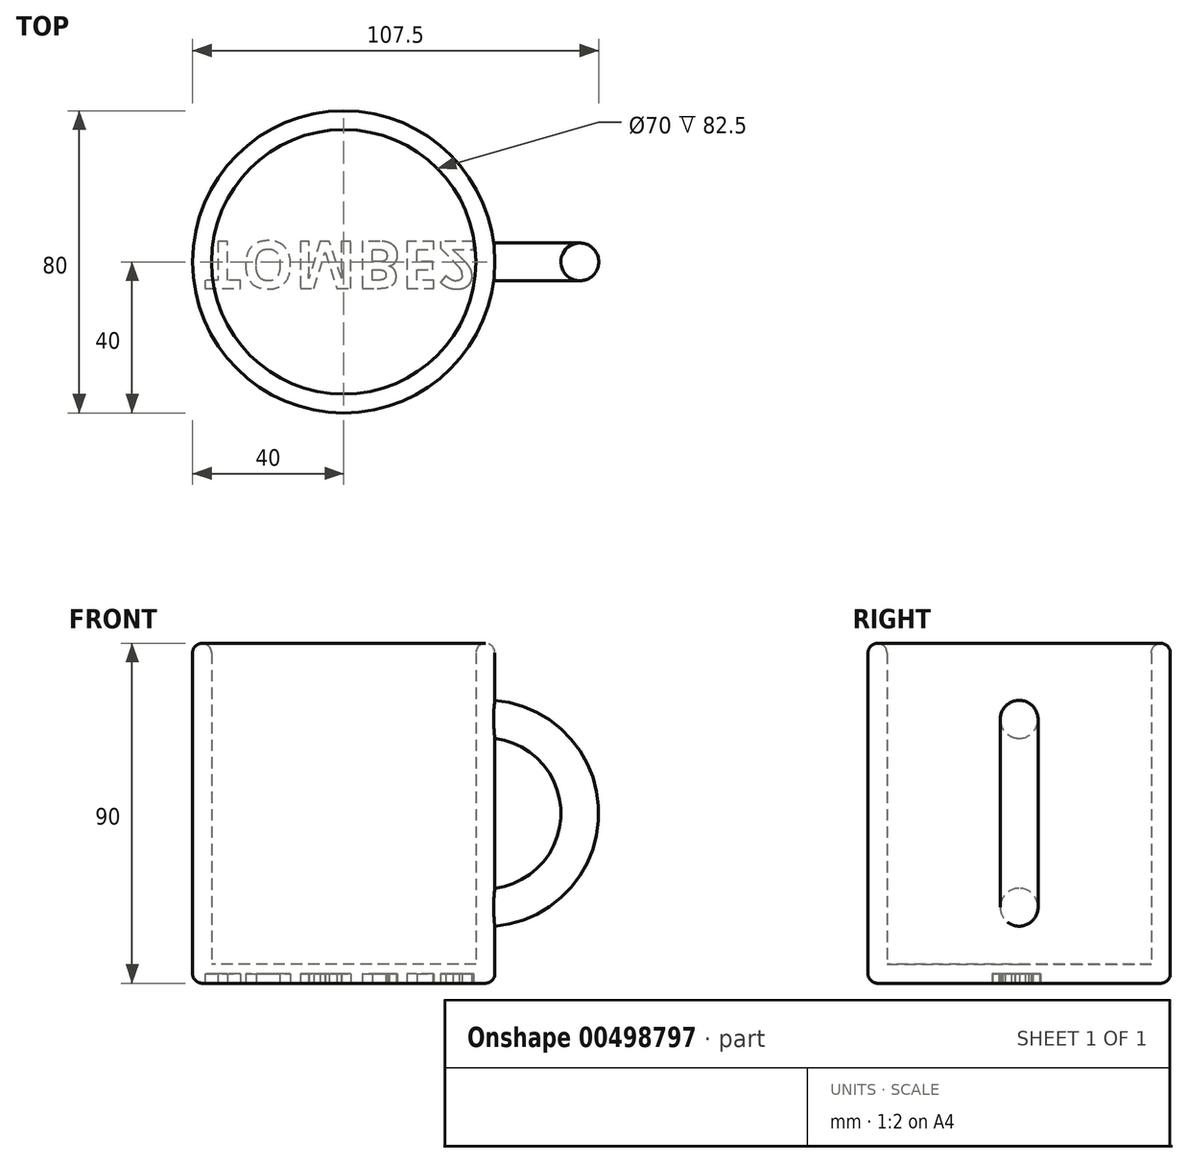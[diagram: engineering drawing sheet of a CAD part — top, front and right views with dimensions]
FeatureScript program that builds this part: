
annotation { "Feature Type Name" : "Feature", "Feature Type Description" : "" }
export const myFeature = defineFeature(function(context is Context, id is Id, definition is map)
    precondition{}
    {
        {
            var Q0;
            Q0=qCreatedBy(makeId("Top.planeOp"),FACE);
            var sketch = newSketch(context, id + "F0", { "sketchPlane" : qUnion([Q0])});
            skCircle(sketch, "E0", {"center": v(0, 0) * mm, "radius": 40 * mm});
            skSolve(sketch);
        }
        {
            var Q0;
            Q0=makeQuery(id+"F0.imprint","IMPRINT",FACE,{"disambiguationData":[TD([[makeQuery(id+"F0.imprint","IMPRINT",EDGE,{"derivedFrom":sQuery(id+"F0.wireOp",EDGE,"E0")}),1.0]])]});
            extrude(context, id + "F1", {"entities" : qUnion([Q0]), "depth" : 90 * mm});
        }
        {
            var Q0;
            Q0=makeQuery(id+"F1.opExtrude","CAP_FACE",FACE,{"disambiguationData":[OSD([sQuery(id+"F0.wireOp",EDGE,"E0")])],"isStart":false});
            shell(context, id + "F2", {"entities" : qUnion([Q0]), "thickness" : 5 * mm});
        }
        {
            var Q0;
            Q0=qCreatedBy(makeId("Right.planeOp"),FACE);
            cPlane(context, id + "F3", {"entities" : qUnion([Q0]), "cplaneType" : CPlaneType.OFFSET, "offset" : 37.5 * mm, "width" : 150 * mm, "height" : 150 * mm});
        }
        {
            var Q0;
            Q0=qCreatedBy(id+"F3.planeOp",FACE);
            var sketch = newSketch(context, id + "F4", { "sketchPlane" : qUnion([Q0])});
            skCircle(sketch, "E1", {"center": v(0, 70) * mm, "radius": 5 * mm});
            skLineSegment(sketch, "E2", {"start": v(0, 45) * mm, "end": v(30.4, 45) * mm});
            skSolve(sketch);
        }
        {
            var Q0;
            Q0 = qSketchRegion(id + "F4", true);
            var Q1;
            Q1=sQuery(id+"F4.wireOp",EDGE,"E2");
            revolve(context, id + "F5", {"operationType" : NewBodyOperationType.ADD, "entities" : qUnion([Q0]), "axis" : qUnion([Q1]), "revolveType" : RevolveType.ONE_DIRECTION, "angle" : 180 * degree});
        }
        {
            var Q0;
            Q0=makeQuery(id+"F1.opExtrude","CAP_EDGE",EDGE,{"disambiguationData":[OSD([sQuery(id+"F0.wireOp",EDGE,"E0")])],"isStart":false});
            var Q1;
            {var subQ0=sQuery(id+"F0.wireOp",EDGE,"E0");Q1=makeQuery(id+"F2.opShell","OFFSET_EDGE",EDGE,{"disambiguationData":[OSD([subQ0]),TDD([makeQuery(id+"F1.opExtrude","CAP_EDGE",EDGE,{"disambiguationData":[OSD([subQ0])],"isStart":false})])]});}
            var Q2;
            Q2=makeQuery(id+"F1.opExtrude","CAP_EDGE",EDGE,{"disambiguationData":[OSD([sQuery(id+"F0.wireOp",EDGE,"E0")])],"isStart":true});
            fillet(context, id + "F6", {"entities" : qUnion([Q0, Q1, Q2]), "radius" : 2.5 * mm, "tangentPropagation" : true, "allowEdgeOverflow" : false});
        }
        {
            var Q0;
            Q0=makeQuery(id+"F1.opExtrude","CAP_FACE",FACE,{"disambiguationData":[OSD([sQuery(id+"F0.wireOp",EDGE,"E0")])],"isStart":true});
            var sketch = newSketch(context, id + "F7", { "sketchPlane" : qUnion([Q0])});
            skText(sketch, "E3", { "text": "TOMBE2", "fontName": "OpenSans-Bold.ttf"});
            const initialGuessF7  = {"E3": [-0.0371, -0.00546, 1, 0, 0.01258]};
            skSetInitialGuess(sketch, initialGuessF7);
            skSolve(sketch);
        }
        {
            var Q0;
            Q0 = qSketchRegion(id + "F7", true);
            extrude(context, id + "F8", {"entities" : qUnion([Q0]), "operationType" : NewBodyOperationType.REMOVE, "oppositeDirection" : true, "depth" : 2.5 * mm});
        }
    });
